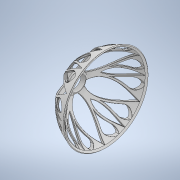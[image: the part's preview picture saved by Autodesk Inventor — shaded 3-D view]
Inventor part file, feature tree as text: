
AUTODESK INVENTOR PART (.ipt)
format: ipt  version: 2020 (Build 240168000, 168)  size: 3,128,320 bytes
history: native  units: mm
features: fillet x7, pattern_circular x4, sketch x2, revolve x1, extrude x1
ambient origin geometry x8: Origin, YZ Plane, XZ Plane, XY Plane, X Axis, Y Axis, Z Axis, Center Point
bodies: Solid1 (feature_tree)
feature tree (15):
  revolve  "Revolution1"  [1 undecoded]
  sketch  "Sketch2"  dims[d7=65.0mm d8=1.0mm d10=0.0mm d11=0.0mm d14=90.0deg d15=3.0mm d23=0.0mm d24=0.0mm d27=30.0mm d28=30.0mm d44=3.0mm d45=4.0mm d47=0.0mm d49=50.0mm d53=45.0deg d56=2.0mm d57=65.0mm d62=25.0mm d63=128.0mm d67=0.0mm d68=60.0deg d69=25.0mm d70=0.0mm d71=3.0mm d72=3.0mm d94=30.0deg d95=25.0mm d96=25.0mm d97=0.0mm d98=3.0mm d99=3.0mm d100=50.0mm d101=0.0mm d105=115.555556mm d106=15.0mm d107=5.0mm d108=5.0mm d109=15.0mm d110=2.0mm d111=60.0mm d112=360.0deg d114=1.5mm d115=0.5mm d116=0.4mm d117=0.4mm d118=0.5mm d119=60.0mm d120=360.0deg d122=60.0mm d123=360.0deg d125=60.0mm d126=360.0deg d128=66.324788mm d25=0.5mm d26=0.872665mm d87=0.5mm d88=0.872665mm d89=0.5mm d90=0.872665mm]
  fillet  "Fillet2"  [1 undecoded]
  extrude  "Extrusion5"  Depth=1.0mm
  fillet  "Fillet3"  [1 undecoded]
  pattern_circular  "Circular Pattern5"  [2 undecoded]
  fillet  "Fillet4"  [1 undecoded]
  fillet  "Fillet5"  Radius=3.0mm
  fillet  "Fillet6"  [1 undecoded]
  fillet  "Fillet7"  [1 undecoded]
  fillet  "Fillet8"  Radius=30.0mm
  pattern_circular  "Circular Pattern6"  Count=3  [1 undecoded]
  pattern_circular  "Circular Pattern7"  [2 undecoded]
  pattern_circular  "Circular Pattern8"  [2 undecoded]
  sketch  "Sketch1"  dims[d0=11.0mm d1=7.0mm d4=90.0deg]
note: 13 required parameter values undecoded (feature->parameter linkage not recoverable at this tier; creation-order binding heuristic only, values carry confidence <= 0.55)